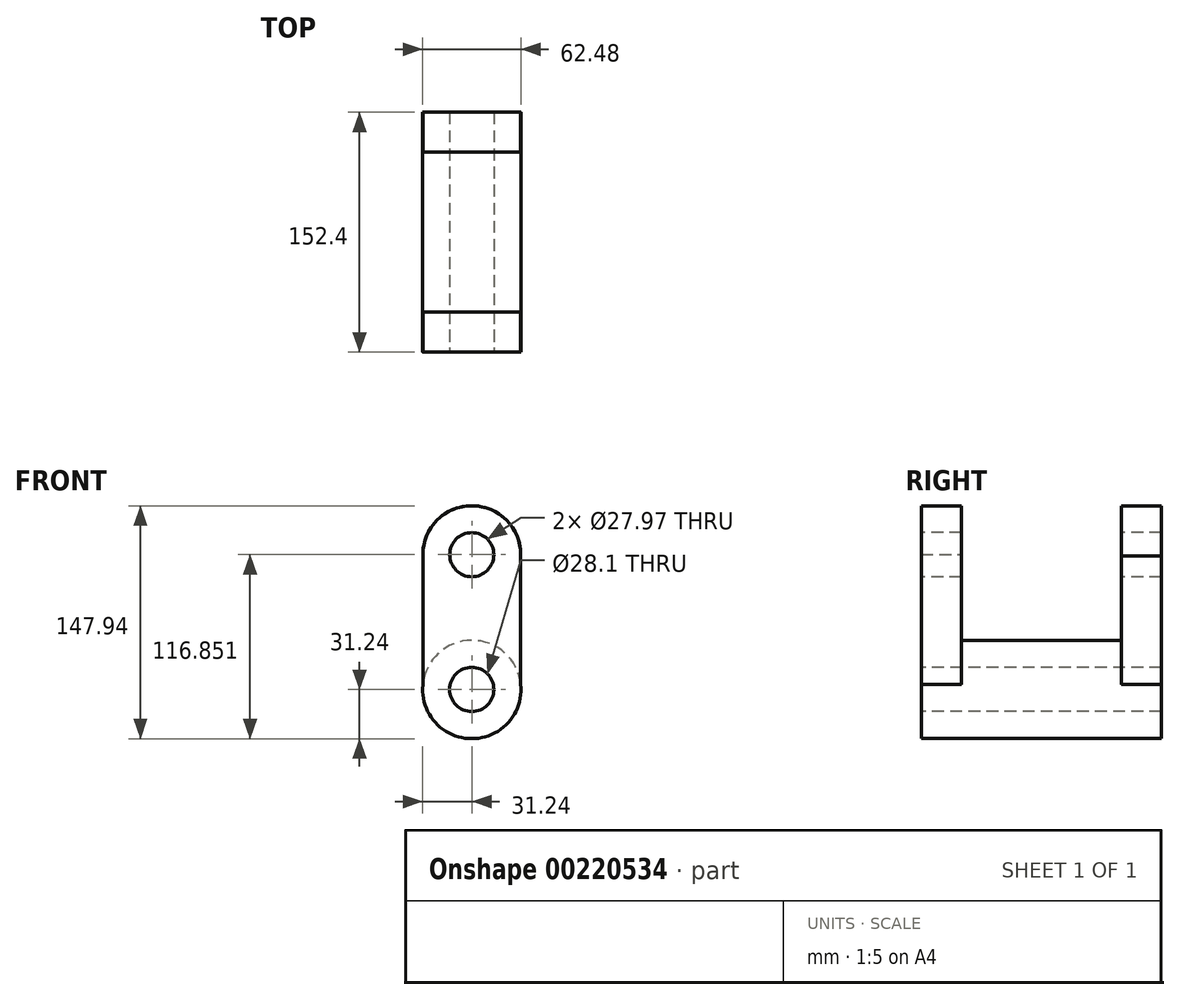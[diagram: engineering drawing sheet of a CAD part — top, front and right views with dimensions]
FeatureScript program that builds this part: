
annotation { "Feature Type Name" : "Feature", "Feature Type Description" : "" }
export const myFeature = defineFeature(function(context is Context, id is Id, definition is map)
    precondition{}
    {
        {
            var Q0;
            Q0=qCreatedBy(makeId("Front.planeOp"),FACE);
            var sketch = newSketch(context, id + "F0", { "sketchPlane" : qUnion([Q0])});
            skCircle(sketch, "E0", {"center": v(0, 0) * mm, "radius": 31.24 * mm});
            skSolve(sketch);
        }
        {
            var Q0;
            Q0=makeQuery(id+"F0.imprint","IMPRINT",FACE,{"disambiguationData":[TD([[makeQuery(id+"F0.imprint","IMPRINT",EDGE,{"derivedFrom":sQuery(id+"F0.wireOp",EDGE,"E0")}),1.0]])]});
            var sketch = newSketch(context, id + "F1", { "sketchPlane" : qUnion([Q0])});
            skLineSegment(sketch, "E1.bottom", {"start": v(-31.1, 0) * mm, "end": v(0, 0) * mm});
            skLineSegment(sketch, "E1.top", {"start": v(-31.1, 85.61) * mm, "end": v(0, 85.61) * mm});
            skLineSegment(sketch, "E1.left", {"start": v(-31.1, 0) * mm, "end": v(-31.1, 85.61) * mm});
            skLineSegment(sketch, "E1.right", {"start": v(0, 0) * mm, "end": v(0, 85.61) * mm});
            skLineSegment(sketch, "E2.bottom", {"start": v(31.08, 0) * mm, "end": v(0, 0) * mm});
            skLineSegment(sketch, "E2.top", {"start": v(31.08, 85.61) * mm, "end": v(0, 85.61) * mm});
            skLineSegment(sketch, "E2.left", {"start": v(31.08, 0) * mm, "end": v(31.08, 85.61) * mm});
            skSolve(sketch);
        }
        {
            var Q0;
            Q0=makeQuery(id+"F0.imprint","IMPRINT",FACE,{"disambiguationData":[TD([[makeQuery(id+"F0.imprint","IMPRINT",EDGE,{"derivedFrom":sQuery(id+"F0.wireOp",EDGE,"E0")}),1.0]])]});
            extrude(context, id + "F2", {"entities" : qUnion([Q0]), "depth" : 25.4 * mm});
        }
        {
            var Q0;
            {var subQ0=sQuery(id+"F1.wireOp",EDGE,"E2.top");Q0=makeQuery(id+"F1.imprint","IMPRINT",FACE,{"disambiguationData":[TD([[makeQuery(id+"F1.imprint","IMPRINT",EDGE,{"derivedFrom":subQ0}),1.0]])]});}
            var Q1;
            {var subQ0=sQuery(id+"F1.wireOp",EDGE,"E1.top");Q1=makeQuery(id+"F1.imprint","IMPRINT",FACE,{"disambiguationData":[TD([[makeQuery(id+"F1.imprint","IMPRINT",EDGE,{"derivedFrom":subQ0}),-1.0]])]});}
            extrude(context, id + "F3", {"entities" : qUnion([Q0, Q1]), "operationType" : NewBodyOperationType.ADD, "depth" : 25.4 * mm});
        }
        {
            var Q0;
            Q0=makeQuery(id+"F0.imprint","IMPRINT",FACE,{"disambiguationData":[TD([[makeQuery(id+"F0.imprint","IMPRINT",EDGE,{"derivedFrom":sQuery(id+"F0.wireOp",EDGE,"E0")}),1.0]])]});
            extrude(context, id + "F4", {"entities" : qUnion([Q0]), "operationType" : NewBodyOperationType.ADD, "oppositeDirection" : true, "depth" : 50.8 * mm});
        }
        {
            var Q0;
            {var subQ0=sQuery(id+"F0.wireOp",EDGE,"E0");Q0=makeQuery(id+"F3.boolean.opBoolean","MERGE",FACE,{"derivedFrom":[makeQuery(id+"F2.opExtrude","CAP_FACE",FACE,{"disambiguationData":[OSD([subQ0])],"isStart":false}),makeQuery(id+"F3.opExtrude","CAP_FACE",FACE,{"disambiguationData":[OSD([subQ0,sQuery(id+"F1.wireOp",EDGE,"E1.top"),sQuery(id+"F1.wireOp",EDGE,"E1.left"),sQuery(id+"F1.wireOp",EDGE,"E2.top"),sQuery(id+"F1.wireOp",EDGE,"E2.left")])],"isStart":false})]});}
            var sketch = newSketch(context, id + "F5", { "sketchPlane" : qUnion([Q0])});
            skCircle(sketch, "E3", {"center": v(0, 0) * mm, "radius": 14.05 * mm});
            skSolve(sketch);
        }
        {
            var Q0;
            Q0=makeQuery(id+"F5.imprint","IMPRINT",FACE,{"disambiguationData":[TD([[makeQuery(id+"F5.imprint","IMPRINT",EDGE,{"derivedFrom":sQuery(id+"F5.wireOp",EDGE,"E3")}),1.0]])]});
            extrude(context, id + "F6", {"entities" : qUnion([Q0]), "operationType" : NewBodyOperationType.REMOVE, "endBound" : BoundingType.THROUGH_ALL, "oppositeDirection" : true, "depth" : 25.4 * mm});
        }
        {
            var Q0;
            Q0=makeQuery(id+"F2.opExtrude","SWEPT_BODY",BODY,{"disambiguationData":[OSD([sQuery(id+"F0.wireOp",EDGE,"E0")])]});
            var Q1;
            Q1=makeQuery(id+"F4.opExtrude","CAP_FACE",FACE,{"disambiguationData":[OSD([sQuery(id+"F0.wireOp",EDGE,"E0")])],"isStart":false});
            mirror(context, id + "F7", {"operationType" : NewBodyOperationType.ADD, "entities" : qUnion([Q0]), "mirrorPlane" : qUnion([Q1])});
        }
        {
            var Q0;
            Q0=makeQuery(id+"F3.opExtrude","SWEPT_FACE",FACE,{"disambiguationData":[OSD([sQuery(id+"F1.wireOp",EDGE,"E1.top"),sQuery(id+"F1.wireOp",EDGE,"E2.top")])]});
            var sketch = newSketch(context, id + "F8", { "sketchPlane" : qUnion([Q0])});
            skLineSegment(sketch, "E4.bottom", {"start": v(31.08, 0) * mm, "end": v(0, 0) * mm});
            skLineSegment(sketch, "E4.top", {"start": v(31.08, -25.4) * mm, "end": v(0, -25.4) * mm});
            skLineSegment(sketch, "E4.left", {"start": v(31.08, 0) * mm, "end": v(31.08, -25.4) * mm});
            skLineSegment(sketch, "E4.right", {"start": v(0, 0) * mm, "end": v(0, -25.4) * mm});
            skSolve(sketch);
        }
        {
            var Q0;
            Q0=makeQuery(id+"F8.imprint","IMPRINT",FACE,{"disambiguationData":[TD([[makeQuery(id+"F8.imprint","IMPRINT",EDGE,{"derivedFrom":sQuery(id+"F8.wireOp",EDGE,"E4.bottom")}),1.0]])]});
            var Q1;
            Q1=sQuery(id+"F8.wireOp",EDGE,"E4.right");
            revolve(context, id + "F9", {"operationType" : NewBodyOperationType.ADD, "entities" : qUnion([Q0]), "axis" : qUnion([Q1]), "revolveType" : RevolveType.FULL});
        }
        {
            var Q0;
            Q0=makeQuery(id+"F7.opPattern","COPY",FACE,{"derivedFrom":makeQuery(id+"F3.opExtrude","SWEPT_FACE",FACE,{"disambiguationData":[OSD([sQuery(id+"F1.wireOp",EDGE,"E1.top"),sQuery(id+"F1.wireOp",EDGE,"E2.top")])]}),"instanceName":"1"});
            var sketch = newSketch(context, id + "F10", { "sketchPlane" : qUnion([Q0])});
            skLineSegment(sketch, "E5.bottom", {"start": v(-31.1, 101.6) * mm, "end": v(0, 101.6) * mm});
            skLineSegment(sketch, "E5.top", {"start": v(-31.1, 127) * mm, "end": v(0, 127) * mm});
            skLineSegment(sketch, "E5.left", {"start": v(-31.1, 101.6) * mm, "end": v(-31.1, 127) * mm});
            skLineSegment(sketch, "E5.right", {"start": v(0, 101.6) * mm, "end": v(0, 127) * mm});
            skSolve(sketch);
        }
        {
            var Q0;
            Q0=makeQuery(id+"F10.imprint","IMPRINT",FACE,{"disambiguationData":[TD([[makeQuery(id+"F10.imprint","IMPRINT",EDGE,{"derivedFrom":sQuery(id+"F10.wireOp",EDGE,"E5.bottom")}),-1.0]])]});
            var Q1;
            Q1=sQuery(id+"F10.wireOp",EDGE,"E5.right");
            revolve(context, id + "F11", {"operationType" : NewBodyOperationType.ADD, "entities" : qUnion([Q0]), "axis" : qUnion([Q1]), "revolveType" : RevolveType.FULL});
        }
        {
            var Q0;
            {var subQ0=sQuery(id+"F0.wireOp",EDGE,"E0");Q0=makeQuery(id+"F9.boolean.opBoolean","MERGE",FACE,{"derivedFrom":[makeQuery(id+"F3.boolean.opBoolean","MERGE",FACE,{"derivedFrom":[makeQuery(id+"F2.opExtrude","CAP_FACE",FACE,{"disambiguationData":[OSD([subQ0])],"isStart":false}),makeQuery(id+"F3.opExtrude","CAP_FACE",FACE,{"disambiguationData":[OSD([subQ0,sQuery(id+"F1.wireOp",EDGE,"E1.top"),sQuery(id+"F1.wireOp",EDGE,"E1.left"),sQuery(id+"F1.wireOp",EDGE,"E2.top"),sQuery(id+"F1.wireOp",EDGE,"E2.left")])],"isStart":false})]}),makeQuery(id+"F9.opRevolve","SWEPT_FACE",FACE,{"disambiguationData":[OSD([sQuery(id+"F8.wireOp",EDGE,"E4.top")])]})]});}
            var sketch = newSketch(context, id + "F12", { "sketchPlane" : qUnion([Q0])});
            skCircle(sketch, "E6", {"center": v(0, 85.61) * mm, "radius": 13.98 * mm});
            skSolve(sketch);
        }
        {
            var Q0;
            Q0=makeQuery(id+"F12.imprint","IMPRINT",FACE,{"disambiguationData":[TD([[makeQuery(id+"F12.imprint","IMPRINT",EDGE,{"derivedFrom":sQuery(id+"F12.wireOp",EDGE,"E6")}),1.0]])]});
            extrude(context, id + "F13", {"entities" : qUnion([Q0]), "operationType" : NewBodyOperationType.REMOVE, "endBound" : BoundingType.THROUGH_ALL, "oppositeDirection" : true, "depth" : 25.4 * mm});
        }
    });
